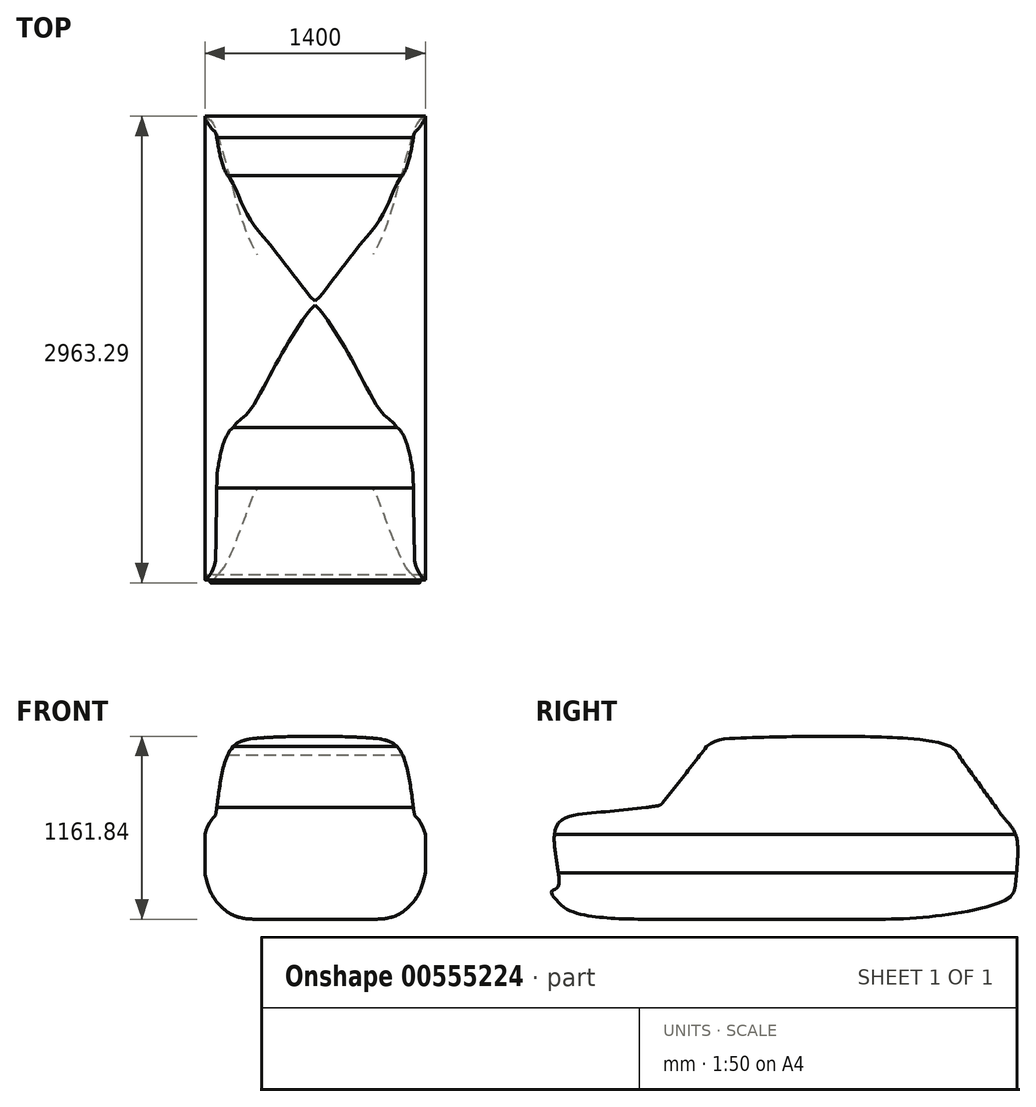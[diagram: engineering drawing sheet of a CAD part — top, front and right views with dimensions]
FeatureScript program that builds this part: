
annotation { "Feature Type Name" : "Feature", "Feature Type Description" : "" }
export const myFeature = defineFeature(function(context is Context, id is Id, definition is map)
    precondition{}
    {
        {
            var Q0;
            Q0=qCreatedBy(makeId("Right.planeOp"),FACE);
            var sketch = newSketch(context, id + "F0", { "sketchPlane" : qUnion([Q0])});
            skLineSegment(sketch, "E0", {"start": v(-3362.3, 0) * mm, "end": v(5418.32, 0) * mm});
            skPoint(sketch, "E0.endSnap0", {"position": v(5418.32, -198.64) * mm});
            skCircle(sketch, "E1", {"center": v(0, 254.72) * mm, "radius": 260.24 * mm, "construction": true});
            skLineSegment(sketch, "E2", {"start": v(1668.34, 317.25) * mm, "end": v(392.06, 317.25) * mm, "construction": true});
            skArc(sketch, "E3", {"start": v(392.06, 317.25) * mm, "mid": v(336.6, 335.33) * mm, "end": v(302.45, 382.64) * mm, "construction": true});
            skArc(sketch, "E4", {"start": v(302.45, 382.64) * mm, "mid": v(4.6, 596.25) * mm, "end": v(-286.04, 372.95) * mm, "construction": true});
            skArc(sketch, "E5", {"start": v(-286.04, 372.95) * mm, "mid": v(-302.7, 347.67) * mm, "end": v(-330.84, 336.52) * mm, "construction": true});
            skArc(sketch, "E6", {"start": v(1668.34, 317.25) * mm, "mid": v(1731.23, 337.96) * mm, "end": v(1769.5, 391.99) * mm, "construction": true});
            skArc(sketch, "E7", {"start": v(1769.5, 391.99) * mm, "mid": v(2096.22, 602.93) * mm, "end": v(2360.08, 317.25) * mm, "construction": true});
            skCircle(sketch, "E8", {"center": v(2049.08, 270.67) * mm, "radius": 261.9 * mm, "construction": true});
            skArc(sketch, "E9", {"start": v(2360.08, 317.25) * mm, "mid": v(2453.63, 333.98) * mm, "end": v(2505.59, 413.56) * mm, "construction": true});
            skLineSegment(sketch, "E10", {"start": v(2145.84, 1240.11) * mm, "end": v(2384.72, 907.9) * mm});
            skFitSpline(sketch, "E11", {"points": [v(2384.72, 907.9) * mm, v(2413.94, 867.26) * mm, v(2488.44, 776.35) * mm, v(2520, 671.47) * mm, v(2505.59, 413.56) * mm], "startDerivative": vector(194.39, -196.9) * mm, "endDerivative": vector(-80.97, -798.52) * mm});
            skFitSpline(sketch, "E12", {"points": [v(2145.84, 1240.11) * mm, v(2112.08, 1284.66) * mm, v(1809.35, 1350.05) * mm, v(717.13, 1350.05) * mm, v(603.3, 1333.1) * mm, v(545.18, 1296.77) * mm], "startDerivative": vector(-251.1, 478.92) * mm, "endDerivative": vector(-543.82, -386.16) * mm});
            skLineSegment(sketch, "E13", {"start": v(545.18, 1296.77) * mm, "end": v(265.8, 939.57) * mm});
            skLineSegment(sketch, "E14", {"start": v(234.05, 920.96) * mm, "end": v(160.78, 909.64) * mm});
            skFitSpline(sketch, "E15", {"points": [v(160.78, 909.64) * mm, v(-189.5, 875.02) * mm, v(-330, 852.62) * mm, v(-419.61, 758.94) * mm, v(-393.14, 427) * mm, v(-419.61, 390.34) * mm, v(-442.01, 374.05) * mm, v(-378.88, 290.55) * mm], "startDerivative": vector(-1713.85, -174.5) * mm, "endDerivative": vector(798.93, -817.25) * mm});
            skFitSpline(sketch, "E16", {"points": [v(-378.88, 290.55) * mm, v(-330.84, 336.52) * mm], "startDerivative": vector(39.56, 46.07) * mm, "endDerivative": vector(60.57, 4.36) * mm, "construction": true});
            skPoint(sketch, "E17.visualSharp", {"position": v(253.6, 923.98) * mm});
            skArc(sketch, "E17.filletArc", {"start": v(234.05, 920.96) * mm, "mid": v(251.7, 927.23) * mm, "end": v(265.8, 939.57) * mm});
            skFitSpline(sketch, "E18", {"points": [v(2505.59, 413.56) * mm, v(2472.18, 341.62) * mm, v(1641.69, 200.42) * mm], "startDerivative": vector(-32.45, -320) * mm, "endDerivative": vector(-1423.03, 0) * mm});
            skLineSegment(sketch, "E19", {"start": v(289.6, 200.42) * mm, "end": v(1641.69, 200.42) * mm});
            skFitSpline(sketch, "E20", {"points": [v(-378.88, 290.55) * mm, v(289.6, 200.42) * mm], "startDerivative": vector(284.75, -291.27) * mm, "endDerivative": vector(674.53, 0) * mm});
            skPoint(sketch, "E21", {"position": v(2612, -1596.48) * mm});
            skPoint(sketch, "E22", {"position": v(-512.37, -1596.48) * mm});
            skSolve(sketch);
        }
        {
            var Q0;
            Q0 = qSketchRegion(id + "F0", true);
            extrude(context, id + "F1", {"entities" : qUnion([Q0]), "endBound" : BoundingType.SYMMETRIC, "depth" : 1400 * mm, "offsetDistance" : 25 * mm});
        }
        {
            var Q0;
            Q0=qCreatedBy(makeId("Front.planeOp"),FACE);
            var sketch = newSketch(context, id + "F2", { "sketchPlane" : qUnion([Q0])});
            skLineSegment(sketch, "E23", {"start": v(-7226.8, -341.5) * mm, "end": v(1553.81, -341.5) * mm});
            skPoint(sketch, "E23.endSnap0", {"position": v(1553.81, -240.77) * mm});
            skLineSegment(sketch, "E24", {"start": v(0, 1362.26) * mm, "end": v(-694.04, 1362.26) * mm, "construction": true});
            skFitSpline(sketch, "E25.0", {"points": [v(0, 1240.11) * mm, v(0, 1280.83) * mm, v(0, 1321.55) * mm, v(0, 1362.26) * mm], "construction": true});
            skFitSpline(sketch, "E26", {"points": [v(0, 1362.26) * mm, v(360.17, 1351.04) * mm, v(547.27, 1259.75) * mm, v(632.84, 862.04) * mm, v(645.03, 845.85) * mm, v(699.76, 738.92) * mm, v(681.94, 419.9) * mm, v(597.18, 281.28) * mm, v(461.42, 207.5) * mm, v(0, 200.42) * mm], "startDerivative": vector(2978.56, 0) * mm, "endDerivative": vector(-3730.07, -330.08) * mm});
            skLineSegment(sketch, "E27", {"start": v(0, 1240.11) * mm, "end": v(0, 1194.63) * mm, "construction": true});
            skFitSpline(sketch, "E28.MirrorCS", {"points": [v(0, 1362.26) * mm, v(-360.17, 1351.04) * mm, v(-547.27, 1259.75) * mm, v(-632.84, 862.04) * mm, v(-645.03, 845.85) * mm, v(-699.76, 738.92) * mm, v(-681.94, 419.9) * mm, v(-597.18, 281.28) * mm, v(-461.42, 207.5) * mm, v(0, 200.42) * mm], "startDerivative": vector(-2978.56, 0) * mm, "endDerivative": vector(3730.07, -330.08) * mm});
            skLineSegment(sketch, "E29.0", {"start": v(700, 200.42) * mm, "end": v(-700, 200.42) * mm, "construction": true});
            skLineSegment(sketch, "E30", {"start": v(-367.01, 200.42) * mm, "end": v(367.01, 200.42) * mm});
            skSolve(sketch);
        }
        {
            var Q0;
            Q0 = qSketchRegion(id + "F2", true);
            extrude(context, id + "F3", {"entities" : qUnion([Q0]), "operationType" : NewBodyOperationType.INTERSECT, "endBound" : BoundingType.THROUGH_ALL, "oppositeDirection" : true, "depth" : 25 * mm, "offsetDistance" : 25 * mm, "hasSecondDirection" : true, "secondDirectionBound" : SecondDirectionBoundingType.THROUGH_ALL, "secondDirectionOppositeDirection" : false, "secondDirectionDepth" : 25 * mm});
        }
        {
            var Q0;
            Q0=qCreatedBy(makeId("Right.planeOp"),FACE);
            cPlane(context, id + "F4", {"entities" : qUnion([Q0]), "cplaneType" : CPlaneType.OFFSET, "offset" : (1179 / 2) * mm, "width" : 150 * mm, "height" : 150 * mm});
        }
    });
